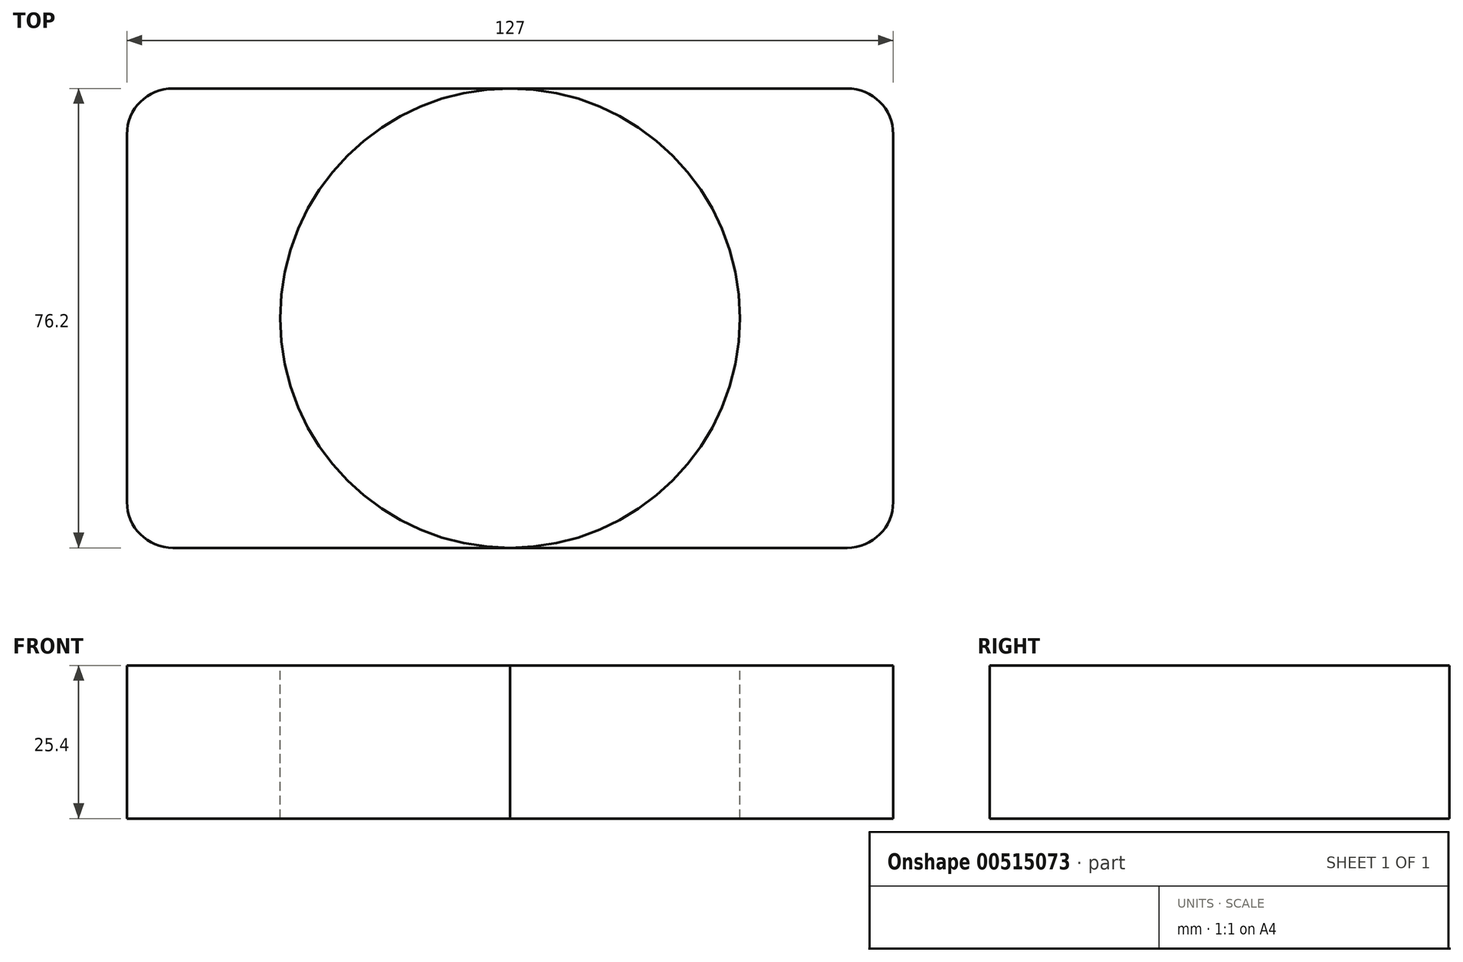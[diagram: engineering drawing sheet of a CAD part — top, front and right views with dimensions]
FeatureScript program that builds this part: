
annotation { "Feature Type Name" : "Feature", "Feature Type Description" : "" }
export const myFeature = defineFeature(function(context is Context, id is Id, definition is map)
    precondition{}
    {
        {
            var Q0;
            Q0=qCreatedBy(makeId("Top.planeOp"),FACE);
            var sketch = newSketch(context, id + "F0", { "sketchPlane" : qUnion([Q0])});
            skLineSegment(sketch, "E0.bottom", {"start": v(63.5, 38.1) * mm, "end": v(-63.5, 38.1) * mm});
            skLineSegment(sketch, "E0.top", {"start": v(63.5, -38.1) * mm, "end": v(-63.5, -38.1) * mm});
            skLineSegment(sketch, "E0.left", {"start": v(63.5, 38.1) * mm, "end": v(63.5, -38.1) * mm});
            skLineSegment(sketch, "E0.right", {"start": v(-63.5, 38.1) * mm, "end": v(-63.5, -38.1) * mm});
            skPoint(sketch, "E0.middle", {"position": v(0, 0) * mm});
            skSolve(sketch);
        }
        {
            var Q0;
            Q0=makeQuery(id+"F0.imprint","IMPRINT",FACE,{"disambiguationData":[TD([[makeQuery(id+"F0.imprint","IMPRINT",EDGE,{"derivedFrom":sQuery(id+"F0.wireOp",EDGE,"E0.bottom")}),1.0]])]});
            extrude(context, id + "F1", {"entities" : qUnion([Q0]), "oppositeDirection" : true, "depth" : 25.4 * mm, "offsetDistance" : 25.4 * mm});
        }
        {
            var Q0;
            Q0=makeQuery(id+"F1.opExtrude","SWEPT_EDGE",EDGE,{"disambiguationData":[OSD([sQuery(id+"F0.wireOp",EDGE,"E0.top"),sQuery(id+"F0.wireOp",EDGE,"E0.left")])]});
            var Q1;
            Q1=makeQuery(id+"F1.opExtrude","SWEPT_EDGE",EDGE,{"disambiguationData":[OSD([sQuery(id+"F0.wireOp",EDGE,"E0.bottom"),sQuery(id+"F0.wireOp",EDGE,"E0.left")])]});
            var Q2;
            Q2=makeQuery(id+"F1.opExtrude","SWEPT_EDGE",EDGE,{"disambiguationData":[OSD([sQuery(id+"F0.wireOp",EDGE,"E0.top"),sQuery(id+"F0.wireOp",EDGE,"E0.right")])]});
            var Q3;
            Q3=makeQuery(id+"F1.opExtrude","SWEPT_EDGE",EDGE,{"disambiguationData":[OSD([sQuery(id+"F0.wireOp",EDGE,"E0.bottom"),sQuery(id+"F0.wireOp",EDGE,"E0.right")])]});
            fillet(context, id + "F2", {"entities" : qUnion([Q0, Q1, Q2, Q3]), "radius" : 7.62 * mm, "tangentPropagation" : true, "allowEdgeOverflow" : false});
        }
        {
            var Q0;
            Q0=makeQuery(id+"F1.opExtrude","CAP_FACE",FACE,{"disambiguationData":[OSD([sQuery(id+"F0.wireOp",EDGE,"E0.bottom"),sQuery(id+"F0.wireOp",EDGE,"E0.top"),sQuery(id+"F0.wireOp",EDGE,"E0.left"),sQuery(id+"F0.wireOp",EDGE,"E0.right")])],"isStart":true});
            var sketch = newSketch(context, id + "F3", { "sketchPlane" : qUnion([Q0])});
            skCircle(sketch, "E1", {"center": v(0, 0) * mm, "radius": 38.1 * mm});
            skSolve(sketch);
        }
        {
            var Q0;
            {var subQ0=sQuery(id+"F3.wireOp",EDGE,"E1");var subQ1=makeQuery(id+"F3.imprint","INTERSECT",VERTEX,{"derivedFrom":[makeQuery(id+"F1.opExtrude","CAP_EDGE",EDGE,{"disambiguationData":[OSD([sQuery(id+"F0.wireOp",EDGE,"E0.bottom")])],"isStart":true}),subQ0]});Q0=makeQuery(id+"F3.imprint","IMPRINT",FACE,{"disambiguationData":[TD([[makeQuery(id+"F3.imprint","IMPRINT",EDGE,{"disambiguationData":[TD([[subQ1,-1.0]])],"derivedFrom":subQ0}),1.0]])]});}
            extrude(context, id + "F4", {"entities" : qUnion([Q0]), "operationType" : NewBodyOperationType.REMOVE, "oppositeDirection" : true, "depth" : 76.2 * mm, "offsetDistance" : 25.4 * mm});
        }
    });
